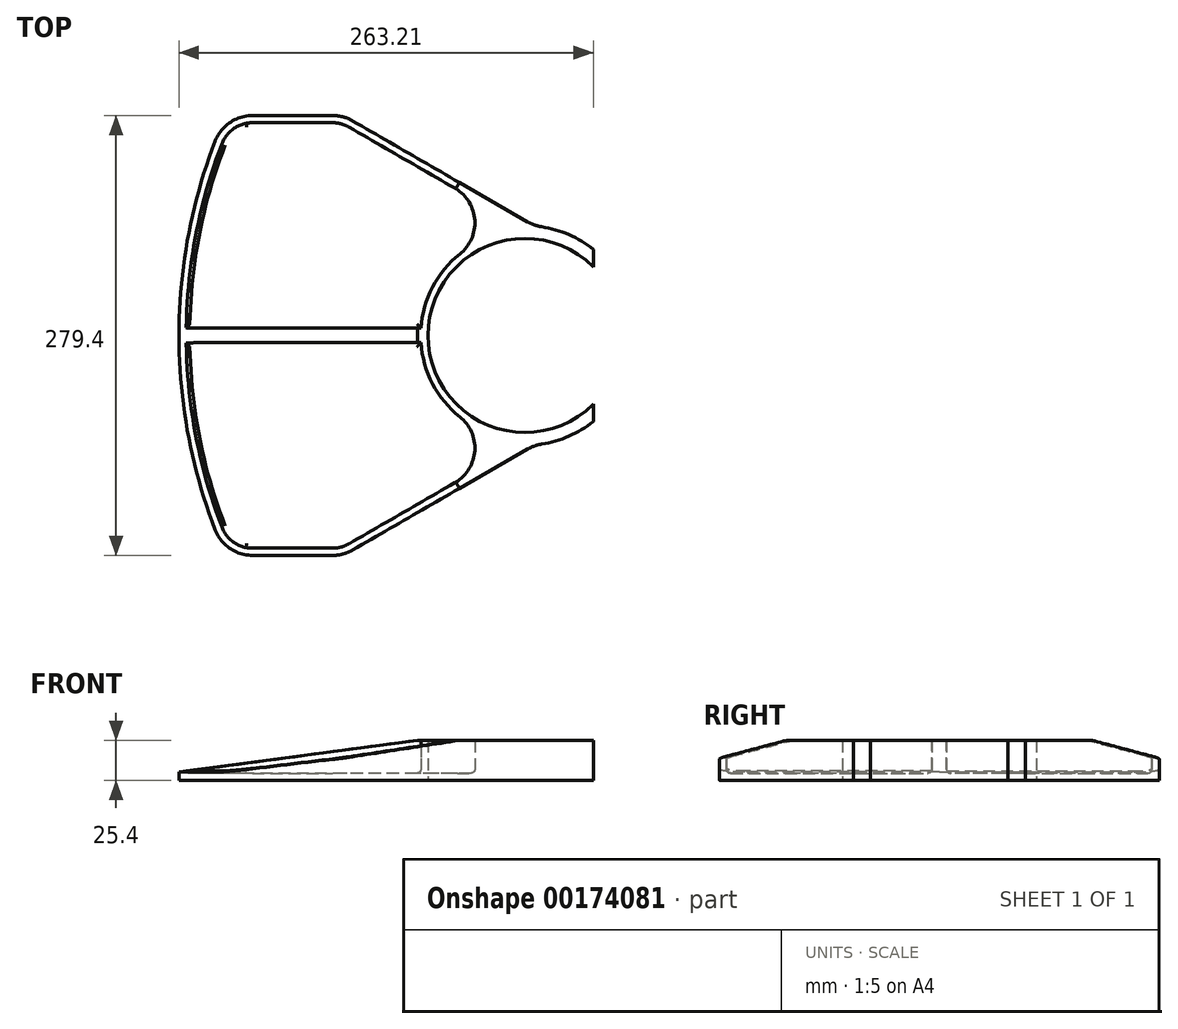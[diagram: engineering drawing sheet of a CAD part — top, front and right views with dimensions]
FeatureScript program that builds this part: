
annotation { "Feature Type Name" : "Feature", "Feature Type Description" : "" }
export const myFeature = defineFeature(function(context is Context, id is Id, definition is map)
    precondition{}
    {
        {
            var Q0;
            Q0=qCreatedBy(makeId("Top.planeOp"),FACE);
            var sketch = newSketch(context, id + "F0", { "sketchPlane" : qUnion([Q0])});
            skCircle(sketch, "E0", {"center": v(0, 0) * mm, "radius": 123.19 * mm, "construction": true});
            skArc(sketch, "E1", {"start": v(-196.72, 123.44) * mm, "mid": v(-213.91, 62.78) * mm, "end": v(-219.71, 0) * mm});
            skArc(sketch, "E2.converted", {"start": v(43.5, 43.61) * mm, "mid": v(-23.6, 56.9) * mm, "end": v(-61.6, 0) * mm});
            skArc(sketch, "E3", {"start": v(25.6, -64.99) * mm, "mid": v(30.35, -62.91) * mm, "end": v(34.92, -60.5) * mm});
            skLineSegment(sketch, "E4.trimOffspring", {"start": v(1.68, 72.16) * mm, "end": v(-109.4, 136.3) * mm});
            skArc(sketch, "E5.trimOffspring", {"start": v(43.5, 54.65) * mm, "mid": v(27.96, 64) * mm, "end": v(10.54, 69.05) * mm});
            skLineSegment(sketch, "E6", {"start": v(27.2, -55.26) * mm, "end": v(27.57, -53.08) * mm, "construction": true});
            skLineSegment(sketch, "E7", {"start": v(43.5, -43.61) * mm, "end": v(43.5, 43.61) * mm, "construction": true});
            skLineSegment(sketch, "E8.trimOffspring", {"start": v(27.57, -53.08) * mm, "end": v(43.5, -43.61) * mm, "construction": true});
            skLineSegment(sketch, "E9", {"start": v(-122.1, 139.7) * mm, "end": v(-173.02, 139.7) * mm, "construction": true});
            skLineSegment(sketch, "E10", {"start": v(-173.02, 139.7) * mm, "end": v(-115.3, 139.7) * mm});
            skPoint(sketch, "E11.orphan", {"position": v(-172.9, 172.95) * mm});
            skLineSegment(sketch, "E12", {"start": v(-61.6, 0) * mm, "end": v(-219.71, 0) * mm});
            skArc(sketch, "E13.trimOffspring", {"start": v(17.51, -59.05) * mm, "mid": v(31.47, -52.95) * mm, "end": v(43.5, -43.61) * mm});
            skPoint(sketch, "E14.orphan", {"position": v(-173.77, -171.45) * mm});
            skPoint(sketch, "E15.visualSharp", {"position": v(6.15, 69.58) * mm});
            skArc(sketch, "E15.filletArc", {"start": v(4.96, 70.26) * mm, "mid": v(6.33, 69.68) * mm, "end": v(7.8, 69.42) * mm});
            skArc(sketch, "E16.filletArc", {"start": v(1.68, 72.16) * mm, "mid": v(5.97, 70.2) * mm, "end": v(10.54, 69.05) * mm});
            skArc(sketch, "E17.filletArc", {"start": v(-109.4, 136.3) * mm, "mid": v(-115.53, 138.83) * mm, "end": v(-122.1, 139.7) * mm});
            skArc(sketch, "E18.filletArc", {"start": v(-173.02, 139.7) * mm, "mid": v(-187.4, 135.25) * mm, "end": v(-196.72, 123.44) * mm});
            skLineSegment(sketch, "E19", {"start": v(43.5, 43.61) * mm, "end": v(43.5, 54.65) * mm});
            skSolve(sketch);
        }
        {
            var Q0;
            Q0=qSketchRegion(id+"F0",true);
            extrude(context, id + "F1", {"entities" : qUnion([Q0]), "depth" : 25.4 * mm});
        }
        {
            var Q0;
            Q0=makeQuery(id+"F1.opExtrude","CAP_FACE",FACE,{"disambiguationData":[OSD([sQuery(id+"F0.wireOp",EDGE,"E1"),sQuery(id+"F0.wireOp",EDGE,"E2.converted"),sQuery(id+"F0.wireOp",EDGE,"E4.trimOffspring"),sQuery(id+"F0.wireOp",EDGE,"E5.trimOffspring"),sQuery(id+"F0.wireOp",EDGE,"x6DmNLtv-4OXp-Px4V-9J6N-d6SHMSUGrN8R"),sQuery(id+"F0.wireOp",EDGE,"E10"),sQuery(id+"F0.wireOp",EDGE,"E12"),sQuery(id+"F0.wireOp",EDGE,"E16.filletArc"),sQuery(id+"F0.wireOp",EDGE,"E17.filletArc"),sQuery(id+"F0.wireOp",EDGE,"E18.filletArc")])],"isStart":false});
            shell(context, id + "F2", {"entities" : qUnion([Q0]), "thickness" : 4.57 * mm});
        }
        {
            var Q0;
            Q0=qCreatedBy(makeId("Front.planeOp"),FACE);
            var sketch = newSketch(context, id + "F3", { "sketchPlane" : qUnion([Q0])});
            skLineSegment(sketch, "E20", {"start": v(0, 0) * mm, "end": v(0, 52.96) * mm, "construction": true});
            skLineSegment(sketch, "E21", {"start": v(123.17, 0) * mm, "end": v(123.17, 94.85) * mm, "construction": true});
            skSolve(sketch);
        }
        {
            var Q0;
            Q0=makeQuery(id+"F1.opExtrude","SWEPT_FACE",FACE,{"disambiguationData":[OSD([sQuery(id+"F0.wireOp",EDGE,"E12")])]});
            var sketch = newSketch(context, id + "F4", { "sketchPlane" : qUnion([Q0])});
            skLineSegment(sketch, "E22", {"start": v(-68.1, 25.4) * mm, "end": v(-219.71, 5.29) * mm});
            skLineSegment(sketch, "E23", {"start": v(-219.71, 25.4) * mm, "end": v(-68.1, 25.4) * mm});
            skLineSegment(sketch, "E24", {"start": v(-219.71, 25.4) * mm, "end": v(-219.71, 5.23) * mm});
            skSolve(sketch);
        }
        {
            var Q0;
            Q0=makeQuery(id+"F2.opShell","OFFSET_EDGE",EDGE,{"disambiguationData":[OSD([sQuery(id+"F0.wireOp",EDGE,"E4.trimOffspring"),sQuery(id+"F0.wireOp",EDGE,"E16.filletArc")])]});
            var Q1;
            Q1=makeQuery(id+"F2.opShell","TWEAK_EDGE",EDGE,{"derivedFrom":[makeQuery(id+"F1.opExtrude","SWEPT_FACE",FACE,{"disambiguationData":[OSD([sQuery(id+"F0.wireOp",EDGE,"E2.converted")])]}),makeQuery(id+"F1.opExtrude","SWEPT_FACE",FACE,{"disambiguationData":[OSD([sQuery(id+"F0.wireOp",EDGE,"E16.filletArc")])]})]});
            fillet(context, id + "F5", {"entities" : qUnion([Q0, Q1]), "radius" : 25.4 * mm, "tangentPropagation" : true, "allowEdgeOverflow" : false});
        }
        {
            var Q0;
            Q0=qSketchRegion(id+"F4",true);
            var Q1;
            Q1=sQuery(id+"F3.wireOp",EDGE,"E21");
            revolve(context, id + "F6", {"operationType" : NewBodyOperationType.REMOVE, "entities" : qUnion([Q0]), "axis" : qUnion([Q1]), "revolveType" : RevolveType.FULL});
        }
        {
            var Q0;
            {var subQ0=sQuery(id+"F0.wireOp",EDGE,"E16.filletArc");var subQ1=sQuery(id+"F0.wireOp",EDGE,"E2.converted");Q0=makeQuery(id+"F5.opFillet","BLEND_EDGE",EDGE,{"blendedFrom":[makeQuery(id+"F2.opShell","TWEAK_EDGE",EDGE,{"derivedFrom":[makeQuery(id+"F1.opExtrude","SWEPT_FACE",FACE,{"disambiguationData":[OSD([subQ1])]}),makeQuery(id+"F1.opExtrude","SWEPT_FACE",FACE,{"disambiguationData":[OSD([subQ0])]})]}),makeQuery(id+"F2.opShell","OFFSET_FACE",FACE,{"disambiguationData":[OSD([sQuery(id+"F0.wireOp",EDGE,"E1"),subQ1,sQuery(id+"F0.wireOp",EDGE,"E4.trimOffspring"),sQuery(id+"F0.wireOp",EDGE,"E5.trimOffspring"),sQuery(id+"F0.wireOp",EDGE,"x6DmNLtv-4OXp-Px4V-9J6N-d6SHMSUGrN8R"),sQuery(id+"F0.wireOp",EDGE,"E10"),sQuery(id+"F0.wireOp",EDGE,"E12"),subQ0,sQuery(id+"F0.wireOp",EDGE,"E17.filletArc"),sQuery(id+"F0.wireOp",EDGE,"E18.filletArc")])]})],"blendedInto":[makeQuery(id+"F2.opShell","OFFSET_FACE",FACE,{"disambiguationData":[OSD([sQuery(id+"F0.wireOp",EDGE,"E1"),subQ1,sQuery(id+"F0.wireOp",EDGE,"E4.trimOffspring"),sQuery(id+"F0.wireOp",EDGE,"E5.trimOffspring"),sQuery(id+"F0.wireOp",EDGE,"x6DmNLtv-4OXp-Px4V-9J6N-d6SHMSUGrN8R"),sQuery(id+"F0.wireOp",EDGE,"E10"),sQuery(id+"F0.wireOp",EDGE,"E12"),subQ0,sQuery(id+"F0.wireOp",EDGE,"E17.filletArc"),sQuery(id+"F0.wireOp",EDGE,"E18.filletArc")])]})]});}
            var Q1;
            {var subQ0=sQuery(id+"F0.wireOp",EDGE,"E12");Q1=makeQuery(id+"F2.opShell","OFFSET_EDGE",EDGE,{"disambiguationData":[OSD([subQ0]),TDD([makeQuery(id+"F1.opExtrude","CAP_EDGE",EDGE,{"disambiguationData":[OSD([subQ0])],"isStart":true})])]});}
            fillet(context, id + "F7", {"entities" : qUnion([Q0, Q1]), "radius" : 2.54 * mm, "tangentPropagation" : true, "allowEdgeOverflow" : false});
        }
        {
            var Q0;
            Q0=makeQuery(id+"F1.opExtrude","SWEPT_BODY",BODY,{"disambiguationData":[OSD([sQuery(id+"F0.wireOp",EDGE,"E1"),sQuery(id+"F0.wireOp",EDGE,"E2.converted"),sQuery(id+"F0.wireOp",EDGE,"E4.trimOffspring"),sQuery(id+"F0.wireOp",EDGE,"E5.trimOffspring"),sQuery(id+"F0.wireOp",EDGE,"x6DmNLtv-4OXp-Px4V-9J6N-d6SHMSUGrN8R"),sQuery(id+"F0.wireOp",EDGE,"E10"),sQuery(id+"F0.wireOp",EDGE,"E12"),sQuery(id+"F0.wireOp",EDGE,"E16.filletArc"),sQuery(id+"F0.wireOp",EDGE,"E17.filletArc"),sQuery(id+"F0.wireOp",EDGE,"E18.filletArc")])]});
            var Q1;
            Q1=qCreatedBy(makeId("Front.planeOp"),FACE);
            mirror(context, id + "F8", {"operationType" : NewBodyOperationType.ADD, "entities" : qUnion([Q0]), "mirrorPlane" : qUnion([Q1])});
        }
    });
